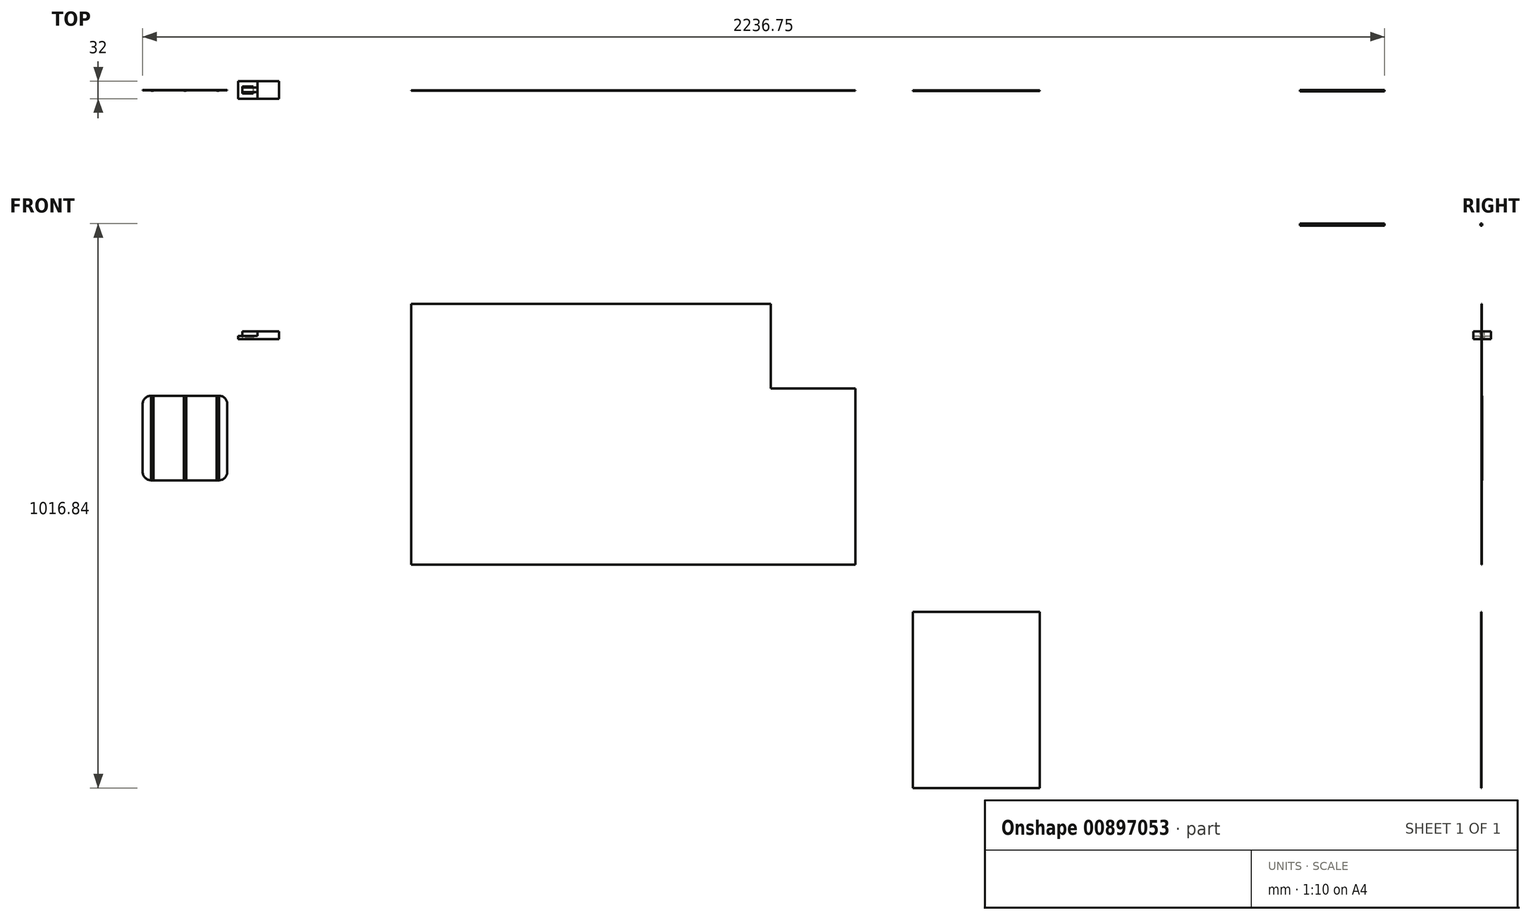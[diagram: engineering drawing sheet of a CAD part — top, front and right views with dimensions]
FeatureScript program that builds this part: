
annotation { "Feature Type Name" : "Feature", "Feature Type Description" : "" }
export const myFeature = defineFeature(function(context is Context, id is Id, definition is map)
    precondition{}
    {
        {
            var Q0;
            Q0=qCreatedBy(makeId("Front.planeOp"),FACE);
            var sketch = newSketch(context, id + "F0", { "sketchPlane" : qUnion([Q0])});
            skLineSegment(sketch, "E0.bottom", {"start": v(766.3, 678.17) * mm, "end": v(888.7, 678.17) * mm});
            skLineSegment(sketch, "E0.top", {"start": v(766.3, 525.77) * mm, "end": v(888.7, 525.77) * mm});
            skLineSegment(sketch, "E0.left", {"start": v(751.3, 663.17) * mm, "end": v(751.3, 540.77) * mm});
            skLineSegment(sketch, "E0.right", {"start": v(903.7, 663.17) * mm, "end": v(903.7, 540.77) * mm});
            skPoint(sketch, "E1.visualSharp", {"position": v(751.3, 678.17) * mm});
            skArc(sketch, "E1.filletArc", {"start": v(766.3, 678.17) * mm, "mid": v(755.7, 673.78) * mm, "end": v(751.3, 663.17) * mm});
            skPoint(sketch, "E2.visualSharp", {"position": v(903.7, 678.17) * mm});
            skArc(sketch, "E2.filletArc", {"start": v(903.7, 663.17) * mm, "mid": v(899.3, 673.78) * mm, "end": v(888.7, 678.17) * mm});
            skPoint(sketch, "E3.visualSharp", {"position": v(903.7, 525.77) * mm});
            skArc(sketch, "E3.filletArc", {"start": v(888.7, 525.77) * mm, "mid": v(899.3, 530.16) * mm, "end": v(903.7, 540.77) * mm});
            skPoint(sketch, "E4.visualSharp", {"position": v(751.3, 525.77) * mm});
            skArc(sketch, "E4.filletArc", {"start": v(751.3, 540.77) * mm, "mid": v(755.7, 530.16) * mm, "end": v(766.3, 525.77) * mm});
            skLineSegment(sketch, "E5.bottom", {"start": v(3038.85, 81858.35) * mm, "end": v(2869.38, 81858.35) * mm});
            skLineSegment(sketch, "E5.top", {"start": v(3038.85, 72650.5) * mm, "end": v(2869.38, 72650.5) * mm});
            skLineSegment(sketch, "E5.left", {"start": v(3038.85, 81858.35) * mm, "end": v(3038.85, 72650.5) * mm});
            skLineSegment(sketch, "E5.right", {"start": v(2869.38, 81858.35) * mm, "end": v(2869.38, 72650.5) * mm});
            skSolve(sketch);
        }
        {
            var Q0;
            Q0=makeQuery(id+"F0.imprint","IMPRINT",FACE,{"disambiguationData":[TD([[makeQuery(id+"F0.imprint","IMPRINT",EDGE,{"derivedFrom":sQuery(id+"F0.wireOp",EDGE,"E0.bottom")}),-1.0]])]});
            extrude(context, id + "F1", {"entities" : qUnion([Q0]), "depth" : 1 * mm, "offsetDistance" : 25 * mm});
        }
        {
            var Q0;
            Q0=makeQuery(id+"F1.opExtrude","CAP_FACE",FACE,{"disambiguationData":[OSD([sQuery(id+"F0.wireOp",EDGE,"E0.bottom"),sQuery(id+"F0.wireOp",EDGE,"E0.top"),sQuery(id+"F0.wireOp",EDGE,"E0.left"),sQuery(id+"F0.wireOp",EDGE,"E0.right"),sQuery(id+"F0.wireOp",EDGE,"E1.filletArc"),sQuery(id+"F0.wireOp",EDGE,"E2.filletArc"),sQuery(id+"F0.wireOp",EDGE,"E3.filletArc"),sQuery(id+"F0.wireOp",EDGE,"E4.filletArc")])],"isStart":false});
            var sketch = newSketch(context, id + "F2", { "sketchPlane" : qUnion([Q0])});
            skLineSegment(sketch, "E6.bottom", {"start": v(1067.58, 689.47) * mm, "end": v(1071.78, 689.47) * mm});
            skLineSegment(sketch, "E6.top", {"start": v(1067.58, 537.07) * mm, "end": v(1071.78, 537.07) * mm});
            skLineSegment(sketch, "E6.left", {"start": v(1067.58, 689.47) * mm, "end": v(1067.58, 537.07) * mm});
            skLineSegment(sketch, "E6.right", {"start": v(1071.78, 689.47) * mm, "end": v(1071.78, 537.07) * mm});
            skLineSegment(sketch, "E7.bottom", {"start": v(1040.2, 697.09) * mm, "end": v(1044.38, 697.09) * mm});
            skLineSegment(sketch, "E7.top", {"start": v(1040.2, 544.69) * mm, "end": v(1044.38, 544.69) * mm});
            skLineSegment(sketch, "E7.left", {"start": v(1040.2, 697.09) * mm, "end": v(1040.2, 544.69) * mm});
            skLineSegment(sketch, "E7.right", {"start": v(1044.38, 697.09) * mm, "end": v(1044.38, 544.69) * mm});
            skLineSegment(sketch, "E8.bottom", {"start": v(998.8, 676.8) * mm, "end": v(1003, 676.8) * mm});
            skLineSegment(sketch, "E8.top", {"start": v(998.8, 524.4) * mm, "end": v(1003, 524.4) * mm});
            skLineSegment(sketch, "E8.left", {"start": v(998.8, 676.8) * mm, "end": v(998.8, 524.4) * mm});
            skLineSegment(sketch, "E8.right", {"start": v(1003, 676.8) * mm, "end": v(1003, 524.4) * mm});
            skSolve(sketch);
        }
        {
            var Q0;
            Q0=makeQuery(id+"F2.imprint","IMPRINT",FACE,{"disambiguationData":[TD([[makeQuery(id+"F2.imprint","IMPRINT",EDGE,{"derivedFrom":sQuery(id+"F2.wireOp",EDGE,"E6.bottom")}),-1.0]])]});
            var Q1;
            Q1=makeQuery(id+"F2.imprint","IMPRINT",FACE,{"disambiguationData":[TD([[makeQuery(id+"F2.imprint","IMPRINT",EDGE,{"derivedFrom":sQuery(id+"F2.wireOp",EDGE,"E7.bottom")}),-1.0]])]});
            var Q2;
            Q2=makeQuery(id+"F2.imprint","IMPRINT",FACE,{"disambiguationData":[TD([[makeQuery(id+"F2.imprint","IMPRINT",EDGE,{"derivedFrom":sQuery(id+"F2.wireOp",EDGE,"E8.bottom")}),-1.0]])]});
            extrude(context, id + "F3", {"entities" : qUnion([Q0, Q1, Q2]), "depth" : 0.5 * mm, "offsetDistance" : 25 * mm});
        }
        {
            var Q0;
            Q0=makeQuery(id+"F3.opExtrude","SWEPT_BODY",BODY,{"disambiguationData":[OSD([sQuery(id+"F2.wireOp",EDGE,"E8.bottom"),sQuery(id+"F2.wireOp",EDGE,"E8.top"),sQuery(id+"F2.wireOp",EDGE,"E8.left"),sQuery(id+"F2.wireOp",EDGE,"E8.right")])]});
            transform(context, id + "F4", {"entities" : qUnion([Q0]), "transformType" : TransformType.TRANSLATION_3D, "dx" : -232.8 * mm, "dy" : 0 * mm, "dz" : 3.3 * mm, "makeCopy" : false});
        }
        {
            var Q0;
            Q0=makeQuery(id+"F3.opExtrude","SWEPT_BODY",BODY,{"disambiguationData":[OSD([sQuery(id+"F2.wireOp",EDGE,"E8.bottom"),sQuery(id+"F2.wireOp",EDGE,"E8.top"),sQuery(id+"F2.wireOp",EDGE,"E8.left"),sQuery(id+"F2.wireOp",EDGE,"E8.right")])]});
            transform(context, id + "F5", {"entities" : qUnion([Q0]), "transformType" : TransformType.TRANSLATION_3D, "dx" : 6E-4000 * mm, "dy" : 0 * mm, "dz" : 0 * mm, "makeCopy" : false});
        }
        {
            var Q0;
            Q0=makeQuery(id+"F3.opExtrude","SWEPT_BODY",BODY,{"disambiguationData":[OSD([sQuery(id+"F2.wireOp",EDGE,"E8.bottom"),sQuery(id+"F2.wireOp",EDGE,"E8.top"),sQuery(id+"F2.wireOp",EDGE,"E8.left"),sQuery(id+"F2.wireOp",EDGE,"E8.right")])]});
            var Q1;
            Q1=makeQuery(id+"F3.opExtrude","CAP_VERTEX",VERTEX,{"disambiguationData":[OSD([sQuery(id+"F2.wireOp",EDGE,"E8.top"),sQuery(id+"F2.wireOp",EDGE,"E8.left")])],"isStart":false});
            var Q2;
            Q2=makeQuery(id+"F1.opExtrude","CAP_EDGE",EDGE,{"disambiguationData":[OSD([sQuery(id+"F0.wireOp",EDGE,"E0.top")])],"isStart":false});
            transform(context, id + "F6", {"entities" : qUnion([Q0]), "transformType" : TransformType.TRANSLATION_ENTITY, "oppositeDirectionEntity" : false, "transformLine" : qUnion([Q1, Q2]), "makeCopy" : false});
        }
        {
            var Q0;
            Q0=makeQuery(id+"F3.opExtrude","SWEPT_BODY",BODY,{"disambiguationData":[OSD([sQuery(id+"F2.wireOp",EDGE,"E8.bottom"),sQuery(id+"F2.wireOp",EDGE,"E8.top"),sQuery(id+"F2.wireOp",EDGE,"E8.left"),sQuery(id+"F2.wireOp",EDGE,"E8.right")])]});
            var Q1;
            Q1=makeQuery(id+"F3.opExtrude","CAP_VERTEX",VERTEX,{"disambiguationData":[OSD([sQuery(id+"F2.wireOp",EDGE,"E8.bottom"),sQuery(id+"F2.wireOp",EDGE,"E8.right")])],"isStart":true});
            var Q2;
            Q2=makeQuery(id+"F1.opExtrude","CAP_VERTEX",VERTEX,{"disambiguationData":[OSD([sQuery(id+"F0.wireOp",EDGE,"E0.bottom"),sQuery(id+"F0.wireOp",EDGE,"E2.filletArc")])],"isStart":false});
            transform(context, id + "F7", {"entities" : qUnion([Q0]), "transformType" : TransformType.TRANSLATION_ENTITY, "oppositeDirectionEntity" : false, "transformLine" : qUnion([Q1, Q2]), "makeCopy" : false});
        }
        {
            var Q0;
            Q0=makeQuery(id+"F3.opExtrude","SWEPT_BODY",BODY,{"disambiguationData":[OSD([sQuery(id+"F2.wireOp",EDGE,"E7.bottom"),sQuery(id+"F2.wireOp",EDGE,"E7.top"),sQuery(id+"F2.wireOp",EDGE,"E7.left"),sQuery(id+"F2.wireOp",EDGE,"E7.right")])]});
            var Q1;
            Q1=sQuery(id+"F2.wireOp",VERTEX,"E7.bottom.start");
            var Q2;
            Q2=makeQuery(id+"F1.opExtrude","CAP_VERTEX",VERTEX,{"disambiguationData":[OSD([sQuery(id+"F0.wireOp",EDGE,"E0.bottom"),sQuery(id+"F0.wireOp",EDGE,"E1.filletArc")])],"isStart":false});
            transform(context, id + "F8", {"entities" : qUnion([Q0]), "transformType" : TransformType.TRANSLATION_ENTITY, "oppositeDirectionEntity" : false, "transformLine" : qUnion([Q1, Q2]), "makeCopy" : false});
        }
        {
            var Q0;
            Q0=sQuery(id+"F2.wireOp",EDGE,"E6.bottom");
            cPoint(context, id + "F9", {"entities" : qUnion([Q0]), "parameter" : 0.5});
        }
        {
            var Q0;
            Q0=makeQuery(id+"F1.opExtrude","CAP_EDGE",EDGE,{"disambiguationData":[OSD([sQuery(id+"F0.wireOp",EDGE,"E0.bottom")])],"isStart":false});
            cPoint(context, id + "F10", {"entities" : qUnion([Q0]), "parameter" : 0.5});
        }
        {
            var Q0;
            Q0=makeQuery(id+"F3.opExtrude","SWEPT_BODY",BODY,{"disambiguationData":[OSD([sQuery(id+"F2.wireOp",EDGE,"E6.bottom"),sQuery(id+"F2.wireOp",EDGE,"E6.top"),sQuery(id+"F2.wireOp",EDGE,"E6.left"),sQuery(id+"F2.wireOp",EDGE,"E6.right")])]});
            var Q1;
            Q1=qCreatedBy(id+"F9",VERTEX);
            var Q2;
            Q2=qCreatedBy(id+"F10",VERTEX);
            transform(context, id + "F11", {"entities" : qUnion([Q0]), "transformType" : TransformType.TRANSLATION_ENTITY, "oppositeDirectionEntity" : false, "transformLine" : qUnion([Q1, Q2]), "makeCopy" : false});
        }
        {
            var Q0;
            Q0=qCreatedBy(makeId("Front.planeOp"),FACE);
            var sketch = newSketch(context, id + "F12", { "sketchPlane" : qUnion([Q0])});
            skLineSegment(sketch, "E9.right", {"start": v(997.16, 786.05) * mm, "end": v(997.16, 780.2) * mm});
            skPoint(sketch, "E10.oppositeSnap0", {"position": v(958.16, 786.05) * mm});
            skLineSegment(sketch, "E10.bottom", {"start": v(997.16, 786.05) * mm, "end": v(958.16, 786.05) * mm});
            skLineSegment(sketch, "E10.top", {"start": v(997.16, 794.2) * mm, "end": v(958.16, 794.2) * mm});
            skLineSegment(sketch, "E10.left", {"start": v(997.16, 786.05) * mm, "end": v(997.16, 794.2) * mm});
            skLineSegment(sketch, "E10.right", {"start": v(958.16, 786.05) * mm, "end": v(958.16, 794.2) * mm});
            skLineSegment(sketch, "E11.bottom", {"start": v(958.16, 790.13) * mm, "end": v(930.77, 790.13) * mm});
            skLineSegment(sketch, "E11.top", {"start": v(958.16, 786.05) * mm, "end": v(930.77, 786.05) * mm});
            skLineSegment(sketch, "E11.left", {"start": v(958.16, 790.13) * mm, "end": v(958.16, 786.05) * mm});
            skLineSegment(sketch, "E11.right", {"start": v(930.77, 790.13) * mm, "end": v(930.77, 786.05) * mm});
            skLineSegment(sketch, "E12", {"start": v(997.16, 780.2) * mm, "end": v(923.16, 780.2) * mm});
            skLineSegment(sketch, "E13", {"start": v(923.16, 780.2) * mm, "end": v(923.16, 786.05) * mm});
            skLineSegment(sketch, "E14", {"start": v(923.16, 786.05) * mm, "end": v(930.77, 786.05) * mm});
            skSolve(sketch);
        }
        {
            var Q0;
            Q0=makeQuery(id+"F12.imprint","IMPRINT",FACE,{"disambiguationData":[TD([[makeQuery(id+"F12.imprint","IMPRINT",EDGE,{"derivedFrom":sQuery(id+"F12.wireOp",EDGE,"E10.bottom")}),-1.0]])]});
            var Q1;
            Q1=makeQuery(id+"F12.imprint","IMPRINT",FACE,{"disambiguationData":[TD([[makeQuery(id+"F12.imprint","IMPRINT",EDGE,{"derivedFrom":sQuery(id+"F12.wireOp",EDGE,"E9.bottom")}),-1.0]])]});
            var Q2;
            Q2=makeQuery(id+"F12.imprint","IMPRINT",FACE,{"disambiguationData":[TD([[makeQuery(id+"F12.imprint","IMPRINT",EDGE,{"derivedFrom":sQuery(id+"F12.wireOp",EDGE,"E9.right")}),-1.0]])]});
            extrude(context, id + "F13", {"entities" : qUnion([Q0, Q1, Q2]), "endBound" : BoundingType.SYMMETRIC, "depth" : 32 * mm, "offsetDistance" : 25 * mm});
        }
        {
            var Q0;
            Q0=makeQuery(id+"F12.imprint","IMPRINT",FACE,{"disambiguationData":[TD([[makeQuery(id+"F12.imprint","IMPRINT",EDGE,{"derivedFrom":sQuery(id+"F12.wireOp",EDGE,"E11.bottom")}),1.0]])]});
            var Q1;
            Q1=sQuery(id+"F12.wireOp",EDGE,"E11.bottom");
            revolve(context, id + "F14", {"surfaceOperationType" : NewSurfaceOperationType.NEW, "entities" : qUnion([Q0]), "axis" : qUnion([Q1]), "revolveType" : RevolveType.ONE_DIRECTION, "angle" : 360 * degree});
        }
        {
            var Q0;
            Q0=makeQuery(id+"F14.opRevolve","SWEPT_FACE",FACE,{"disambiguationData":[OSD([sQuery(id+"F12.wireOp",EDGE,"E11.right")])]});
            var sketch = newSketch(context, id + "F15", { "sketchPlane" : qUnion([Q0])});
            skCircle(sketch, "E15", {"center": v(0, 790.13) * mm, "radius": 7.66 * mm});
            skSolve(sketch);
        }
        {
            var Q0;
            Q0=makeQuery(id+"F15.imprint","IMPRINT",FACE,{"disambiguationData":[TD([[makeQuery(id+"F15.imprint","IMPRINT",EDGE,{"derivedFrom":sQuery(id+"F15.wireOp",EDGE,"E15")}),1.0]])]});
            extrude(context, id + "F16", {"entities" : qUnion([Q0]), "operationType" : NewBodyOperationType.REMOVE, "depth" : -20 * mm, "offsetDistance" : 25 * mm});
        }
        {
            var Q0;
            Q0=makeQuery(id+"F1.opExtrude","CAP_FACE",FACE,{"disambiguationData":[OSD([sQuery(id+"F0.wireOp",EDGE,"E0.bottom"),sQuery(id+"F0.wireOp",EDGE,"E0.top"),sQuery(id+"F0.wireOp",EDGE,"E0.left"),sQuery(id+"F0.wireOp",EDGE,"E0.right"),sQuery(id+"F0.wireOp",EDGE,"E1.filletArc"),sQuery(id+"F0.wireOp",EDGE,"E2.filletArc"),sQuery(id+"F0.wireOp",EDGE,"E3.filletArc"),sQuery(id+"F0.wireOp",EDGE,"E4.filletArc")])],"isStart":false});
            var sketch = newSketch(context, id + "F17", { "sketchPlane" : qUnion([Q0])});
            skLineSegment(sketch, "E16.bottom", {"start": v(1234.72, 843.78) * mm, "end": v(1882.42, 843.78) * mm});
            skLineSegment(sketch, "E16.top", {"start": v(1234.72, 373.88) * mm, "end": v(1882.42, 373.88) * mm});
            skLineSegment(sketch, "E16.left", {"start": v(1234.72, 843.78) * mm, "end": v(1234.72, 373.88) * mm});
            skLineSegment(sketch, "E16.right", {"start": v(1882.42, 843.78) * mm, "end": v(1882.42, 373.88) * mm});
            skLineSegment(sketch, "E17.bottom", {"start": v(1882.42, 373.88) * mm, "end": v(2034.82, 373.88) * mm});
            skLineSegment(sketch, "E17.top", {"start": v(1882.42, 691.38) * mm, "end": v(2034.82, 691.38) * mm});
            skLineSegment(sketch, "E17.left", {"start": v(1882.42, 373.88) * mm, "end": v(1882.42, 691.38) * mm});
            skLineSegment(sketch, "E17.right", {"start": v(2034.82, 373.88) * mm, "end": v(2034.82, 691.38) * mm});
            skSolve(sketch);
        }
        {
            var Q0;
            Q0=makeQuery(id+"F17.imprint","IMPRINT",FACE,{"disambiguationData":[TD([[makeQuery(id+"F17.imprint","IMPRINT",EDGE,{"derivedFrom":sQuery(id+"F17.wireOp",EDGE,"E16.bottom")}),-1.0]])]});
            var Q1;
            Q1=makeQuery(id+"F17.imprint","IMPRINT",FACE,{"disambiguationData":[TD([[makeQuery(id+"F17.imprint","IMPRINT",EDGE,{"derivedFrom":sQuery(id+"F17.wireOp",EDGE,"E17.bottom")}),1.0]])]});
            extrude(context, id + "F18", {"entities" : qUnion([Q0, Q1]), "endBound" : BoundingType.SYMMETRIC, "depth" : 1 * mm, "offsetDistance" : 25.4 * mm});
        }
        {
            var Q0;
            Q0=makeQuery(id+"F18.opExtrude","CAP_FACE",FACE,{"disambiguationData":[OSD([sQuery(id+"F17.wireOp",EDGE,"E16.bottom"),sQuery(id+"F17.wireOp",EDGE,"E16.top"),sQuery(id+"F17.wireOp",EDGE,"E16.left"),sQuery(id+"F17.wireOp",EDGE,"E16.right")])],"isStart":false});
            var sketch = newSketch(context, id + "F19", { "sketchPlane" : qUnion([Q0])});
            skLineSegment(sketch, "E18.bottom", {"start": v(2175.25, 988.19) * mm, "end": v(2988.05, 988.19) * mm});
            skLineSegment(sketch, "E18.top", {"start": v(2175.25, 505.59) * mm, "end": v(2988.05, 505.59) * mm});
            skLineSegment(sketch, "E18.left", {"start": v(2175.25, 988.19) * mm, "end": v(2175.25, 505.59) * mm});
            skLineSegment(sketch, "E18.right", {"start": v(2988.05, 988.19) * mm, "end": v(2988.05, 505.59) * mm});
            skLineSegment(sketch, "E19.bottom", {"start": v(2988.05, 988.19) * mm, "end": v(2835.65, 988.19) * mm});
            skLineSegment(sketch, "E19.top", {"start": v(2988.05, 835.79) * mm, "end": v(2835.65, 835.79) * mm});
            skLineSegment(sketch, "E19.left", {"start": v(2988.05, 988.19) * mm, "end": v(2988.05, 835.79) * mm});
            skLineSegment(sketch, "E19.right", {"start": v(2835.65, 988.19) * mm, "end": v(2835.65, 835.79) * mm});
            skLineSegment(sketch, "E20.bottom", {"start": v(2988.05, 835.79) * mm, "end": v(2984.25, 835.79) * mm});
            skLineSegment(sketch, "E20.top", {"start": v(2988.05, 988.19) * mm, "end": v(2984.25, 988.19) * mm});
            skLineSegment(sketch, "E20.left", {"start": v(2988.05, 835.79) * mm, "end": v(2988.05, 988.19) * mm});
            skLineSegment(sketch, "E20.right", {"start": v(2984.25, 835.79) * mm, "end": v(2984.25, 988.19) * mm});
            skLineSegment(sketch, "E21.bottom", {"start": v(2835.65, 988.19) * mm, "end": v(2988.05, 988.19) * mm});
            skLineSegment(sketch, "E21.top", {"start": v(2835.65, 984.43) * mm, "end": v(2988.05, 984.43) * mm});
            skLineSegment(sketch, "E21.left", {"start": v(2835.65, 988.19) * mm, "end": v(2835.65, 984.43) * mm});
            skLineSegment(sketch, "E21.right", {"start": v(2988.05, 988.19) * mm, "end": v(2988.05, 984.43) * mm});
            skLineSegment(sketch, "E22.bottom", {"start": v(2861.05, 784.99) * mm, "end": v(2905.5, 784.99) * mm});
            skLineSegment(sketch, "E22.top", {"start": v(2861.05, 689.74) * mm, "end": v(2905.5, 689.74) * mm});
            skLineSegment(sketch, "E22.left", {"start": v(2861.05, 784.99) * mm, "end": v(2861.05, 689.74) * mm});
            skLineSegment(sketch, "E22.right", {"start": v(2905.5, 784.99) * mm, "end": v(2905.5, 689.74) * mm});
            skLineSegment(sketch, "E23.bottom", {"start": v(2861.05, 657.99) * mm, "end": v(2905.5, 657.99) * mm});
            skLineSegment(sketch, "E23.top", {"start": v(2861.05, 562.74) * mm, "end": v(2905.5, 562.74) * mm});
            skLineSegment(sketch, "E23.left", {"start": v(2861.05, 657.99) * mm, "end": v(2861.05, 562.74) * mm});
            skLineSegment(sketch, "E23.right", {"start": v(2905.5, 657.99) * mm, "end": v(2905.5, 562.74) * mm});
            skSolve(sketch);
        }
        {
            var Q0;
            Q0=makeQuery(id+"F19.imprint","IMPRINT",FACE,{"disambiguationData":[TD([[makeQuery(id+"F19.imprint","IMPRINT",EDGE,{"derivedFrom":sQuery(id+"F19.wireOp",EDGE,"E18.bottom")}),-1.0]])]});
            var Q1;
            {var subQ5=sQuery(id+"F19.wireOp",EDGE,"E21.left");Q1=makeQuery(id+"F19.imprint","IMPRINT",FACE,{"disambiguationData":[TD([[makeQuery(id+"F19.imprint","IMPRINT",EDGE,{"derivedFrom":subQ5}),1.0]])]});}
            var Q2;
            {var subQ5=sQuery(id+"F19.wireOp",EDGE,"E21.right");Q2=makeQuery(id+"F19.imprint","IMPRINT",FACE,{"disambiguationData":[TD([[makeQuery(id+"F19.imprint","IMPRINT",EDGE,{"derivedFrom":subQ5}),-1.0]])]});}
            var Q3;
            {var subQ0=sQuery(id+"F19.wireOp",EDGE,"E20.bottom");Q3=makeQuery(id+"F19.imprint","IMPRINT",FACE,{"disambiguationData":[TD([[makeQuery(id+"F19.imprint","IMPRINT",EDGE,{"derivedFrom":subQ0}),-1.0]])]});}
            extrude(context, id + "F20", {"entities" : qUnion([Q0, Q1, Q2, Q3]), "endBound" : BoundingType.SYMMETRIC, "depth" : 2.66 * mm, "offsetDistance" : 25.4 * mm});
        }
        {
            var Q0;
            Q0=makeQuery(id+"F18.opExtrude","CAP_FACE",FACE,{"disambiguationData":[OSD([sQuery(id+"F17.wireOp",EDGE,"E16.bottom"),sQuery(id+"F17.wireOp",EDGE,"E16.top"),sQuery(id+"F17.wireOp",EDGE,"E16.left"),sQuery(id+"F17.wireOp",EDGE,"E16.right")])],"isStart":false});
            var sketch = newSketch(context, id + "F21", { "sketchPlane" : qUnion([Q0])});
            skLineSegment(sketch, "E24.bottom", {"start": v(2138.3, 288.85) * mm, "end": v(2366.9, 288.85) * mm});
            skLineSegment(sketch, "E24.top", {"start": v(2138.3, -28.65) * mm, "end": v(2366.9, -28.65) * mm});
            skLineSegment(sketch, "E24.left", {"start": v(2138.3, 288.85) * mm, "end": v(2138.3, -28.65) * mm});
            skLineSegment(sketch, "E24.right", {"start": v(2366.9, 288.85) * mm, "end": v(2366.9, -28.65) * mm});
            skSolve(sketch);
        }
        {
            var Q0;
            Q0=makeQuery(id+"F21.imprint","IMPRINT",FACE,{"disambiguationData":[TD([[makeQuery(id+"F21.imprint","IMPRINT",EDGE,{"derivedFrom":sQuery(id+"F21.wireOp",EDGE,"E24.bottom")}),-1.0]])]});
            extrude(context, id + "F22", {"entities" : qUnion([Q0]), "endBound" : BoundingType.SYMMETRIC, "depth" : 1 * mm, "offsetDistance" : 25.4 * mm});
        }
    });
